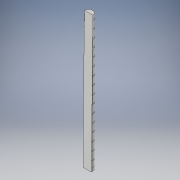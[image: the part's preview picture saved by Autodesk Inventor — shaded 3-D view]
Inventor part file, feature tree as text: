
AUTODESK INVENTOR PART (.ipt)
format: ipt  version: 2018 (Build 220112000, 112)  size: 2,044,928 bytes
history: native  units: in
note: dims shown in document units (in); Inventor stores cm internally (conversion verified against a paired STEP export)
features: sketch x13, extrude x12, plane x7, other x7, reference x3, projected_geometry x3, mirror x2, surface_op x1, loft x1, direct_edit x1
ambient origin geometry x8: Origin, YZ Plane, XZ Plane, XY Plane, X Axis, Y Axis, Z Axis, Center Point
bodies: Solid1 (feature_tree)
feature tree (50):
  extrude  "Extrusion1"  Depth=3.0in
  extrude  "Extrusion2"  Depth=1.0in TaperAngle=0.0deg
  extrude  "Extrusion3"  Depth=3.0in TaperAngle=0.0deg
  extrude  "Extrusion4"  Depth=3.0in TaperAngle=0.0deg
  extrude  "Extrusion5"  Depth=7.25in TaperAngle=0.0deg
  plane  "Work Plane1"
  plane  "Work Plane2"
  mirror  "Mirror1"
  mirror  "Mirror2"
  extrude  "Extrusion6"  Depth=0.25in
  surface_op  "Sculpt1"
  extrude  "Extrusion7"  Depth=2.0in TaperAngle=0.0deg
  extrude  "Extrusion9"  Depth=11.811in TaperAngle=0.0deg
  extrude  "Extrusion10"  TaperAngle=0.0deg  [1 undecoded]
  extrude  "Extrusion13"  Depth=0.3937in
  loft  "Loft1"
  direct_edit  "Direct Edit2"
  extrude  "Extrusion16"  [1 undecoded]
  plane  "Work Plane3"
  plane  "Work Plane4"
  plane  "Work Plane5"
  plane  "Work Plane6"
  plane  "Work Plane7"
  extrude  "Extrusion19"  [1 undecoded]
  sketch  "Sketch1"  dims[d0=1.0in d1=3.0in]
  sketch  "Sketch3"  dims[d2=1.0in d3=0.0in d4=1.0in d5=0.0in]
  sketch  "Sketch4"  dims[d6=1.0in d7=0.0in d8=3.0in d9=0.0in]
  reference  "Reference1"
  sketch  "Sketch5"  dims[d10=0.3in d11=3.0in d12=0.0in]
  reference  "Reference2"
  reference  "Reference3"
  sketch  "Sketch6"  dims[d13=7.25in d14=0.0in d15=7.25in d16=0.0in]
  sketch  "Sketch7"  dims[d19=0.25in d20=0.25in]
  projected_geometry  "Projected Loop1"
  sketch  "Sketch8"  dims[d21=2.0in d22=0.0in d23=2.0in d24=0.0in]
  sketch  "Sketch10"  dims[d36=0.0148in d37=11.811in d38=0.0in]
  sketch  "Sketch11"  dims[d39=0.0074in d40=0.0in d41=90.0deg]
  sketch  "Sketch14"  dims[d42=0.0in d43=90.0deg d44=0.3937in d45=0.374in d46=0.374in]
  sketch  "Sketch15"  dims[d52=0.1969in d53=0.0in d66=-0.3937in]
  projected_geometry  "Projected Loop2"
  other  "Edges1"
  sketch  "Sketch18"  dims[d67=3.937in d68=0.0in]
  projected_geometry  "Projected Loop3"
  sketch  "Sketch23"
  other  "<userpath>\Desktop\spring jig.iam"
  other  "spring jig.iam"
  other  "AR-15 GI Magazine Spring Uncompressed:1"
  other  "Composite1"
  other  "Srf1"
  other  "Scale2"
note: 3 required parameter values undecoded (feature->parameter linkage not recoverable at this tier; creation-order binding heuristic only, values carry confidence <= 0.55)
